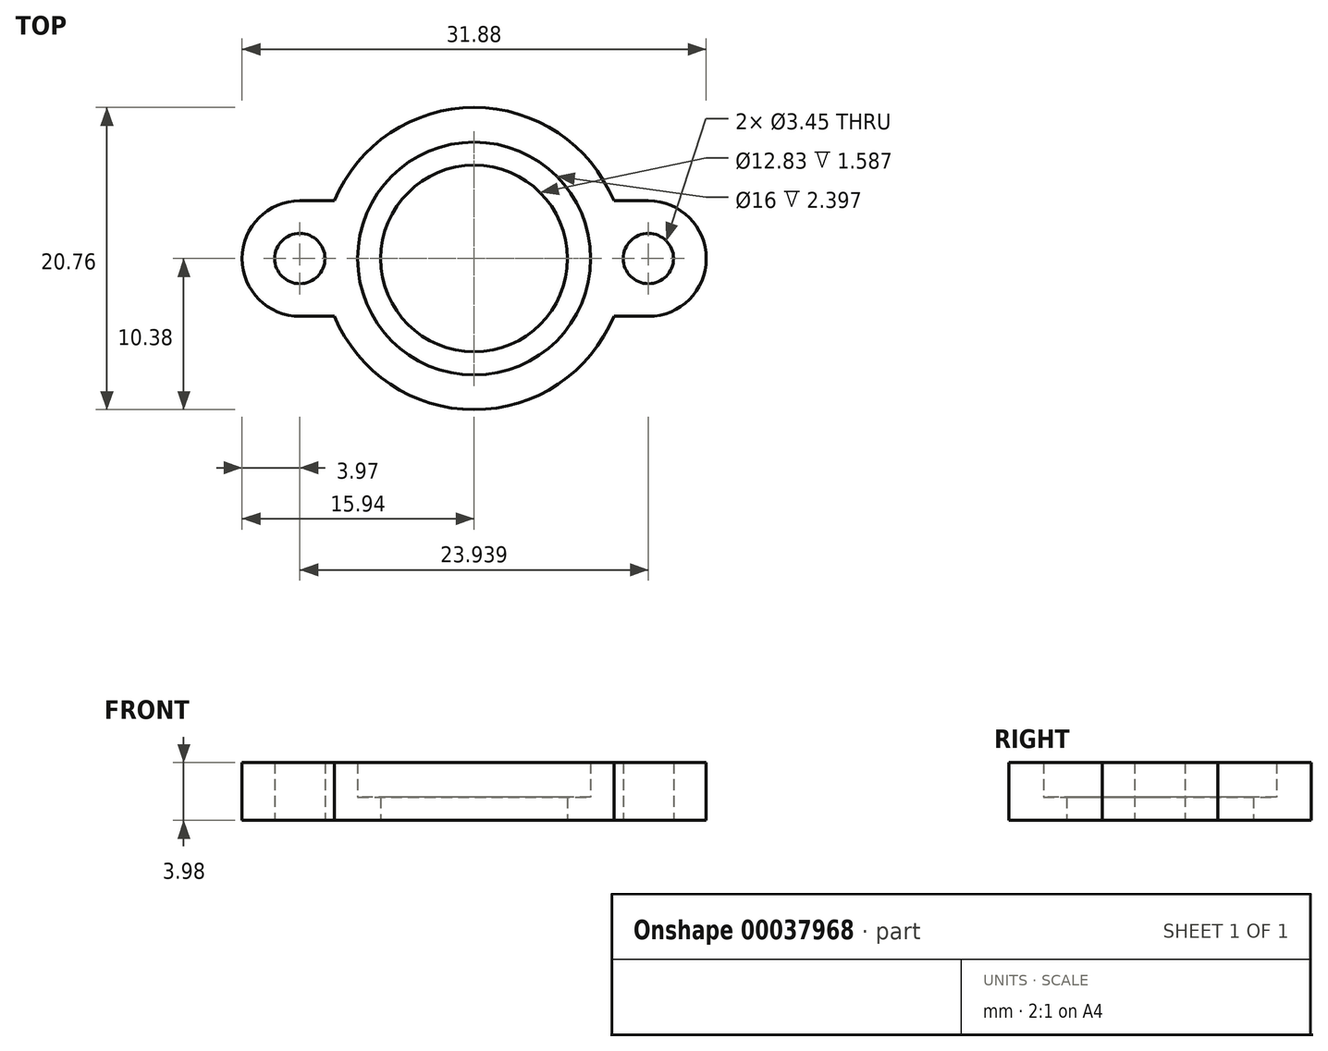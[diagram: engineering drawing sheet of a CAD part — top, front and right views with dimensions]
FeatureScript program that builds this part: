
annotation { "Feature Type Name" : "Feature", "Feature Type Description" : "" }
export const myFeature = defineFeature(function(context is Context, id is Id, definition is map)
    precondition{}
    {
        {
            var Q0;
            Q0=qCreatedBy(makeId("Top.planeOp"),FACE);
            var sketch = newSketch(context, id + "F0", { "sketchPlane" : qUnion([Q0])});
            skLineSegment(sketch, "E0", {"start": v(0, 0) * mm, "end": v(23.94, 0) * mm, "construction": true});
            skCircle(sketch, "E1", {"center": v(0, 0) * mm, "radius": 1.73 * mm});
            skCircle(sketch, "E2", {"center": v(11.97, 0) * mm, "radius": 6.41 * mm});
            skCircle(sketch, "E3", {"center": v(23.94, 0) * mm, "radius": 1.73 * mm});
            skArc(sketch, "E4", {"start": v(0, 3.97) * mm, "mid": v(-3.97, 0) * mm, "end": v(0, -3.97) * mm});
            skArc(sketch, "E5", {"start": v(23.94, -3.97) * mm, "mid": v(27.9, 0) * mm, "end": v(23.94, 3.97) * mm});
            skArc(sketch, "E6", {"start": v(21.56, 3.97) * mm, "mid": v(11.97, 10.38) * mm, "end": v(2.38, 3.97) * mm});
            skArc(sketch, "E7", {"start": v(2.38, -3.97) * mm, "mid": v(11.97, -10.38) * mm, "end": v(21.56, -3.97) * mm});
            skLineSegment(sketch, "E8", {"start": v(0, 3.97) * mm, "end": v(0, -3.97) * mm, "construction": true});
            skLineSegment(sketch, "E9", {"start": v(23.94, 3.97) * mm, "end": v(23.94, -3.97) * mm, "construction": true});
            skLineSegment(sketch, "E10", {"start": v(0, 3.97) * mm, "end": v(2.38, 3.97) * mm});
            skLineSegment(sketch, "E11", {"start": v(0, -3.97) * mm, "end": v(2.38, -3.97) * mm});
            skLineSegment(sketch, "E12", {"start": v(23.94, -3.97) * mm, "end": v(21.56, -3.97) * mm});
            skLineSegment(sketch, "E13", {"start": v(23.94, 3.97) * mm, "end": v(21.56, 3.97) * mm});
            skSolve(sketch);
        }
        {
            var Q0;
            Q0=qSketchRegion(id+"F0",true);
            extrude(context, id + "F1", {"entities" : qUnion([Q0]), "depth" : 1.59 * mm});
        }
        {
            var Q0;
            Q0=makeQuery(id+"F1.opExtrude","CAP_FACE",FACE,{"disambiguationData":[OSD([sQuery(id+"F0.wireOp",EDGE,"E1"),sQuery(id+"F0.wireOp",EDGE,"E2"),sQuery(id+"F0.wireOp",EDGE,"E3"),sQuery(id+"F0.wireOp",EDGE,"E4"),sQuery(id+"F0.wireOp",EDGE,"E5"),sQuery(id+"F0.wireOp",EDGE,"E6"),sQuery(id+"F0.wireOp",EDGE,"E7"),sQuery(id+"F0.wireOp",EDGE,"E10"),sQuery(id+"F0.wireOp",EDGE,"E11"),sQuery(id+"F0.wireOp",EDGE,"E12"),sQuery(id+"F0.wireOp",EDGE,"E13")])],"isStart":false});
            var sketch = newSketch(context, id + "F2", { "sketchPlane" : qUnion([Q0])});
            skCircle(sketch, "E14", {"center": v(11.97, 0) * mm, "radius": 8 * mm});
            skSolve(sketch);
        }
        {
            var Q0;
            Q0=makeQuery(id+"F2.imprint","IMPRINT",FACE,{"disambiguationData":[TD([[makeQuery(id+"F2.imprint","IMPRINT",EDGE,{"derivedFrom":sQuery(id+"F2.wireOp",EDGE,"E14")}),-1.0]])]});
            extrude(context, id + "F3", {"entities" : qUnion([Q0]), "operationType" : NewBodyOperationType.ADD, "depth" : 2.4 * mm});
        }
    });
